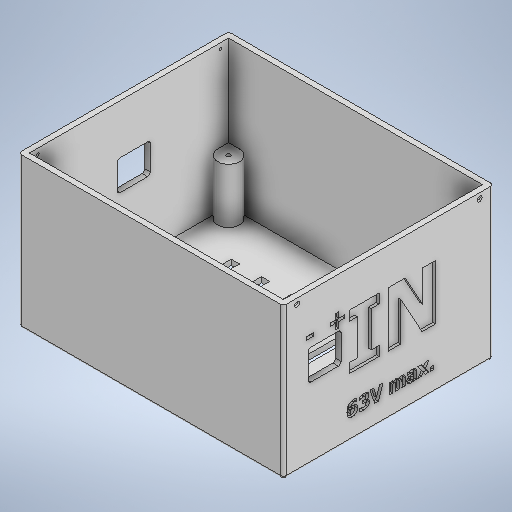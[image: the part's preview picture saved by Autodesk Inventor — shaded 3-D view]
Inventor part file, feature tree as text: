
AUTODESK INVENTOR PART (.ipt)
format: ipt  version: 2025 (Build 290162010, 162A)  size: 635,904 bytes
history: native  units: in
note: dims shown in document units (in); Inventor stores cm internally (conversion verified against a paired STEP export)
features: extrude x10, sketch x10, shell x1, fillet x1, chamfer x1, projected_geometry x1
ambient origin geometry x8: Origin, YZ Plane, XZ Plane, XY Plane, X Axis, Y Axis, Z Axis, Center Point
bodies: Volumenkörper1 (feature_tree)
feature tree (24):
  extrude  "Extrusion1"  Depth=0.1181in
  shell  "Wandung1"  Thickness=0.1181in
  extrude  "Extrusion4"  Depth=0.1181in
  extrude  "Extrusion5"  Depth=0.1181in TaperAngle=0.0deg
  fillet  "Rundung1"  Radius=0.0787in
  extrude  "Extrusion6"  Depth=0.4724in
  chamfer  "Fasen2"  Distance=0.1575in
  extrude  "Extrusion10"  Depth=0.1575in TaperAngle=0.0deg
  extrude  "Extrusion11"  Depth=0.0394in
  extrude  "Extrusion12"  Depth=0.0394in TaperAngle=0.0deg
  extrude  "Extrusion13"  Depth=0.1969in
  extrude  "Extrusion14"  Depth=0.0394in
  extrude  "Extrusion15"  Depth=0.0394in
  sketch  "Skizze1"  dims[d0=2.7756in d1=3.563in d2=0.1181in]
  sketch  "Skizze4"  dims[d3=0.1181in d4=0.1181in]
  sketch  "Skizze5"  dims[d5=0.1181in d6=2.1654in d7=0.0in d8=0.0787in]
  sketch  "Skizze6"  dims[d26=0.2756in d27=0.4724in]
  sketch  "Skizze10"  dims[d29=0.4331in d30=0.1575in d31=0.0in]
  sketch  "Skizze11"  dims[d33=1.2598in d34=0.1575in d35=0.0in]
  projected_geometry  "Projizierte Kontur1"
  sketch  "Skizze12"  dims[d36=0.0394in d40=0.0787in]
  sketch  "Skizze13"  dims[d43=0.0394in d44=0.1575in d45=0.0in]
  sketch  "Skizze14"  dims[d46=0.1969in d47=0.1969in]
  sketch  "Skizze15"  dims[d48=0.0157in d49=0.0787in d50=45.0deg d65=0.9449in d66=0.9449in d67=0.1575in d68=0.1575in d69=0.1575in d70=0.1575in d71=0.1575in d72=0.1575in d73=0.1575in d74=0.1575in d75=0.315in d76=0.7874in d77=0.0in d78=0.0591in d79=0.3937in d80=0.0in d81=0.315in d82=0.315in d83=0.315in d84=0.315in d85=0.315in d86=0.1181in d87=1.5748in d88=0.6791in d89=0.6398in d90=2.1654in d91=0.0in d92=0.0394in d93=0.0in d94=0.0394in d95=0.0in d96=0.0394in d97=0.0in]
